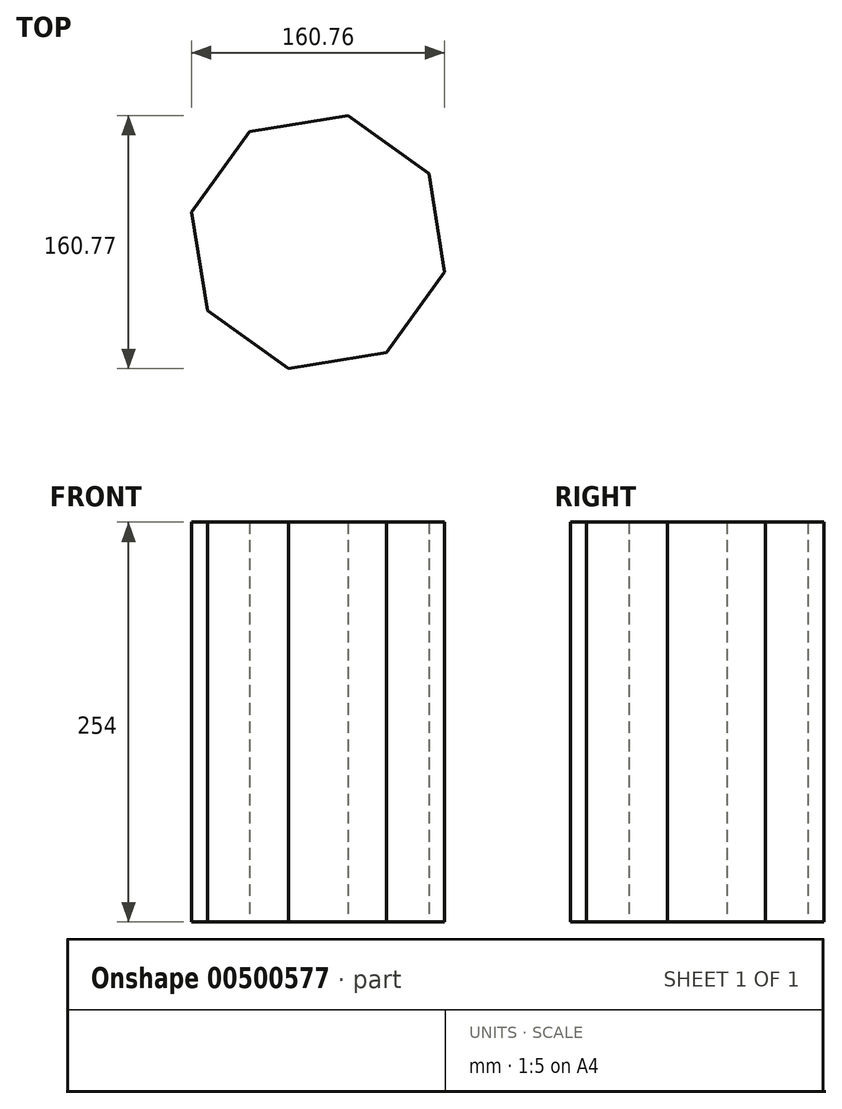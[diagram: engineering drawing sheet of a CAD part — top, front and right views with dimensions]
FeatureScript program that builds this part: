
annotation { "Feature Type Name" : "Feature", "Feature Type Description" : "" }
export const myFeature = defineFeature(function(context is Context, id is Id, definition is map)
    precondition{}
    {
        {
            var Q0;
            Q0=qCreatedBy(makeId("Top.planeOp"),FACE);
            var sketch = newSketch(context, id + "F0", { "sketchPlane" : qUnion([Q0])});
            skPoint(sketch, "E0", {"position": v(-5.54, 8.02) * mm});
            skCircle(sketch, "E1.cCircle", {"center": v(-5.54, 8.02) * mm, "radius": 82.59 * mm, "construction": true});
            skLineSegment(sketch, "E1.0", {"start": v(-48.97, 78.26) * mm, "end": v(13.42, 88.4) * mm});
            skLineSegment(sketch, "E1.1", {"start": v(13.42, 88.4) * mm, "end": v(64.7, 51.45) * mm});
            skLineSegment(sketch, "E1.2", {"start": v(64.7, 51.45) * mm, "end": v(74.84, -10.95) * mm});
            skLineSegment(sketch, "E1.3", {"start": v(74.84, -10.95) * mm, "end": v(37.9, -62.23) * mm});
            skLineSegment(sketch, "E1.4", {"start": v(37.9, -62.23) * mm, "end": v(-24.5, -72.37) * mm});
            skLineSegment(sketch, "E1.5", {"start": v(-24.5, -72.37) * mm, "end": v(-75.78, -35.41) * mm});
            skLineSegment(sketch, "E1.6", {"start": v(-75.78, -35.41) * mm, "end": v(-85.92, 26.98) * mm});
            skLineSegment(sketch, "E1.7", {"start": v(-85.92, 26.98) * mm, "end": v(-48.97, 78.26) * mm});
            skSolve(sketch);
        }
        {
            var Q0;
            Q0 = qSketchRegion(id + "F0", true);
            extrude(context, id + "F1", {"entities" : qUnion([Q0]), "depth" : 254 * mm});
        }
    });
